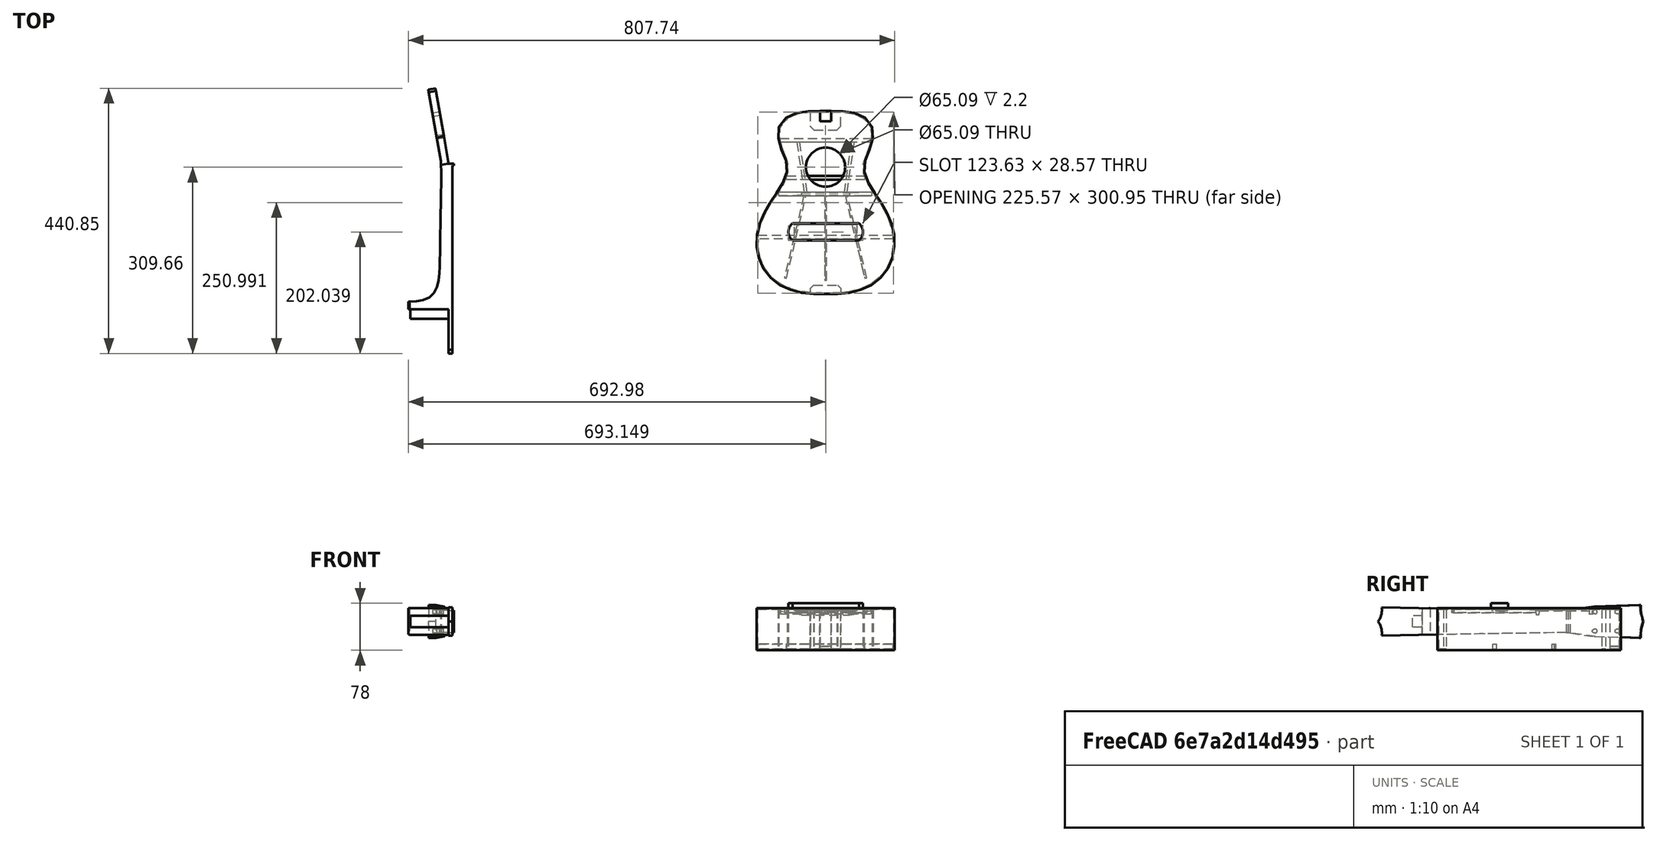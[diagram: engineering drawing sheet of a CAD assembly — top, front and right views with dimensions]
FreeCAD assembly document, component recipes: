
FREECAD ASSEMBLY — COMPONENT RECIPES ("ukulele")

This assembly document has 2 components, labeled P0..P1 below (a component is one placed body or linked part). 2 of them carry a construction recipe — the FreeCAD feature program that regenerates the part from scratch, quoted from this document or its linked companion documents; the rest are supplied as boundary geometry only. No exploded tour is included for this assembly.
COMPONENT P0 — recipe-attached ("kast001", modeled in this document).
Construction recipe (the document's own serialized feature program — sketch geometry with constraints, then the solid features built on it; lengths are millimeters unless a unit is written):

FEATURE [Sketcher::SketchObject] Sketch003  label="vk"
  ArcFitTolerance = 1e-06
  FullyConstrained = false
  MakeInternals = false
  sketch-geometry (68):
    g0: BSplineCurve PolesCount=33 KnotsCount=31 Degree=3 IsPeriodic=0
    g1-g33: Circle [constr] x33 (B-spline internal-alignment scaffolding for g0; pole/knot coordinates omitted)
    g34-g64: GeomPoint [constr] x31 (B-spline internal-alignment scaffolding for g0; pole/knot coordinates omitted)
    g65: BSplineCurve PolesCount=33 KnotsCount=31 Degree=3 IsPeriodic=0
    g66: LineSegment StartX=-9.40108 StartY=93.5875 StartZ=0 EndX=9.40107 EndY=93.5875 EndZ=0
    g67: LineSegment StartX=-0.637124 StartY=-210.927 StartZ=0 EndX=0.637124 EndY=-210.927 EndZ=0
  constraints (73):
    c: InternalAlignment(g1,g0)
    c: Weight(g1) = 1
    c: InternalAlignment(g2,g0)
    c: Equal(g2,g1)
    c: InternalAlignment(g3,g0)
    c: Equal(g3,g1)
    c: InternalAlignment(g4,g0)
    c: Equal(g4,g1)
    c: InternalAlignment(g5,g0)
    c: Equal(g5,g1)
    c: InternalAlignment(g6,g0)
    c: Equal(g6,g1)
    c: InternalAlignment(g7,g0)
    c: Equal(g7,g1)
    c: InternalAlignment(g8,g0)
    c: Equal(g8,g1)
    c: InternalAlignment(g9,g0)
    c: Equal(g9,g1)
    c: InternalAlignment(g10,g0)
    c: Equal(g10,g1)
    c: InternalAlignment(g11,g0)
    c: Equal(g11,g1)
    c: InternalAlignment(g12,g0)
    c: Equal(g12,g1)
    c: InternalAlignment(g13,g0)
    c: Equal(g13,g1)
    c: InternalAlignment(g14,g0)
    c: Equal(g14,g1)
    c: InternalAlignment(g15,g0)
    c: Equal(g15,g1)
    c: InternalAlignment(g16,g0)
    c: Equal(g16,g1)
    c: InternalAlignment(g17,g0)
    c: Equal(g17,g1)
    c: InternalAlignment(g18,g0)
    c: Equal(g18,g1)
    c: InternalAlignment(g19,g0)
    c: Equal(g19,g1)
    c: InternalAlignment(g20,g0)
    c: Equal(g20,g1)
    c: InternalAlignment(g21,g0)
    c: Equal(g21,g1)
    c: InternalAlignment(g22,g0)
    c: Equal(g22,g1)
    c: InternalAlignment(g23,g0)
    c: Equal(g23,g1)
    c: InternalAlignment(g24,g0)
    c: Equal(g24,g1)
    c: InternalAlignment(g25,g0)
    c: Equal(g25,g1)
    c: InternalAlignment(g26,g0)
    c: Equal(g26,g1)
    c: InternalAlignment(g27,g0)
    c: Equal(g27,g1)
    c: InternalAlignment(g28,g0)
    c: Equal(g28,g1)
    c: InternalAlignment(g29,g0)
    c: Equal(g29,g1)
    c: InternalAlignment(g30,g0)
    c: Equal(g30,g1)
    c: InternalAlignment(g31,g0)
    c: Equal(g31,g1)
    c: InternalAlignment(g32,g0)
    c: Equal(g32,g1)
    c: InternalAlignment(g33,g0)
    c: Equal(g33,g1)
    c: InternalAlignment(g34-g64 -> g0) x31
    c: Coincident(g66,g0)
    c: Coincident(g66,g65)
    c: Horizontal(g66)
    c: Coincident(g67,g0)
    c: Coincident(g67,g65)
    c: Horizontal(g67)
FEATURE [PartDesign::Pad] Pad
  Direction = (0,0,1)
  Length = 2.2
  Length2 = 10
  Profile = -> Sketch003
  ReferenceAxis = -> Sketch003 [N_Axis]
  Reversed = true
  Suppressed = false
  Type = 0
  expr: Length = <<dimensies>>.DIKTE_FRONT
FEATURE [Sketcher::SketchObject] Sketch004
  ArcFitTolerance = 1e-06
  AttachmentSupport = -> [XY_Plane001]
  FullyConstrained = true
  MakeInternals = false
  MapMode = 5
  sketch-geometry (1):
    g0: Circle CenterX=0 CenterY=0 CenterZ=0 NormalX=0 NormalY=0 NormalZ=1 AngleXU=0 Radius=32.5435
  constraints (2):
    c: Coincident(g0,g-1)
    c: Diameter(g0) = 65.087
FEATURE [PartDesign::Pocket] Pocket
  BaseFeature = -> Pad
  Direction = (0,0,-1)
  Length = 5
  Length2 = 5
  Profile = -> Sketch004
  ReferenceAxis = -> Sketch004 [N_Axis]
  Suppressed = false
  Type = 2
FEATURE [Sketcher::SketchObject] Sketch005  label="base sketch001"
  ArcFitTolerance = 1e-06
  FullyConstrained = false
  MakeInternals = false
  sketch-geometry (136):
    g0: BSplineCurve PolesCount=33 KnotsCount=31 Degree=3 IsPeriodic=0
    g1-g33: Circle [constr] x33 (B-spline internal-alignment scaffolding for g0; pole/knot coordinates omitted)
    g34-g64: GeomPoint [constr] x31 (B-spline internal-alignment scaffolding for g0; pole/knot coordinates omitted)
    g65: BSplineCurve PolesCount=33 KnotsCount=31 Degree=3 IsPeriodic=0
    g66-g98: Circle [constr] x33 (B-spline internal-alignment scaffolding for g65; pole/knot coordinates omitted)
    g99-g129: GeomPoint [constr] x31 (B-spline internal-alignment scaffolding for g65; pole/knot coordinates omitted)
    g130: BSplineCurve PolesCount=33 KnotsCount=31 Degree=3 IsPeriodic=0
    g131: BSplineCurve PolesCount=33 KnotsCount=31 Degree=3 IsPeriodic=0
    g132: LineSegment StartX=-9.32903 StartY=91.8043 StartZ=0 EndX=9.32903 EndY=91.8043 EndZ=0
    g133: LineSegment StartX=-9.40108 StartY=93.5875 StartZ=0 EndX=9.40107 EndY=93.5875 EndZ=0
    g134: LineSegment StartX=-0.629425 StartY=-209.143 StartZ=0 EndX=0.629425 EndY=-209.143 EndZ=0
    g135: LineSegment StartX=-0.637124 StartY=-210.927 StartZ=0 EndX=0.637124 EndY=-210.927 EndZ=0
  constraints (146):
    c: InternalAlignment(g1,g0)
    c: Weight(g1) = 1
    c: InternalAlignment(g2,g0)
    c: Equal(g2,g1)
    c: InternalAlignment(g3,g0)
    c: Equal(g3,g1)
    c: InternalAlignment(g4,g0)
    c: Equal(g4,g1)
    c: InternalAlignment(g5,g0)
    c: Equal(g5,g1)
    c: InternalAlignment(g6,g0)
    c: Equal(g6,g1)
    c: InternalAlignment(g7,g0)
    c: Equal(g7,g1)
    c: InternalAlignment(g8,g0)
    c: Equal(g8,g1)
    c: InternalAlignment(g9,g0)
    c: Equal(g9,g1)
    c: InternalAlignment(g10,g0)
    c: Equal(g10,g1)
    c: InternalAlignment(g11,g0)
    c: Equal(g11,g1)
    c: InternalAlignment(g12,g0)
    c: Equal(g12,g1)
    c: InternalAlignment(g13,g0)
    c: Equal(g13,g1)
    c: InternalAlignment(g14,g0)
    c: Equal(g14,g1)
    c: InternalAlignment(g15,g0)
    c: Equal(g15,g1)
    c: InternalAlignment(g16,g0)
    c: Equal(g16,g1)
    c: InternalAlignment(g17,g0)
    c: Equal(g17,g1)
    c: InternalAlignment(g18,g0)
    c: Equal(g18,g1)
    c: InternalAlignment(g19,g0)
    c: Equal(g19,g1)
    c: InternalAlignment(g20,g0)
    c: Equal(g20,g1)
    c: InternalAlignment(g21,g0)
    c: Equal(g21,g1)
    c: InternalAlignment(g22,g0)
    c: Equal(g22,g1)
    c: InternalAlignment(g23,g0)
    c: Equal(g23,g1)
    c: InternalAlignment(g24,g0)
    c: Equal(g24,g1)
    c: InternalAlignment(g25,g0)
    c: Equal(g25,g1)
    c: InternalAlignment(g26,g0)
    c: Equal(g26,g1)
    c: InternalAlignment(g27,g0)
    c: Equal(g27,g1)
    c: InternalAlignment(g28,g0)
    c: Equal(g28,g1)
    c: InternalAlignment(g29,g0)
    c: Equal(g29,g1)
    c: InternalAlignment(g30,g0)
    c: Equal(g30,g1)
    c: InternalAlignment(g31,g0)
    c: Equal(g31,g1)
    c: InternalAlignment(g32,g0)
    c: Equal(g32,g1)
    c: InternalAlignment(g33,g0)
    c: Equal(g33,g1)
    c: InternalAlignment(g34-g64 -> g0) x31
    c: InternalAlignment(g66,g65)
    c: Weight(g66) = 1
    c: InternalAlignment(g67,g65)
    c: Equal(g67,g66)
    c: InternalAlignment(g68,g65)
    c: Equal(g68,g66)
    c: InternalAlignment(g69,g65)
    c: Equal(g69,g66)
    c: InternalAlignment(g70,g65)
    c: Equal(g70,g66)
    c: InternalAlignment(g71,g65)
    c: Equal(g71,g66)
    c: InternalAlignment(g72,g65)
    c: Equal(g72,g66)
    c: InternalAlignment(g73,g65)
    c: Equal(g73,g66)
    c: InternalAlignment(g74,g65)
    c: Equal(g74,g66)
    c: InternalAlignment(g75,g65)
    c: Equal(g75,g66)
    c: InternalAlignment(g76,g65)
    c: Equal(g76,g66)
    c: InternalAlignment(g77,g65)
    c: Equal(g77,g66)
    c: InternalAlignment(g78,g65)
    c: Equal(g78,g66)
    c: InternalAlignment(g79,g65)
    c: Equal(g79,g66)
    c: InternalAlignment(g80,g65)
    c: Equal(g80,g66)
    c: InternalAlignment(g81,g65)
    c: Equal(g81,g66)
    c: InternalAlignment(g82,g65)
    c: Equal(g82,g66)
    c: InternalAlignment(g83,g65)
    c: Equal(g83,g66)
    c: InternalAlignment(g84,g65)
    c: Equal(g84,g66)
    c: InternalAlignment(g85,g65)
    c: Equal(g85,g66)
    c: InternalAlignment(g86,g65)
    c: Equal(g86,g66)
    c: InternalAlignment(g87,g65)
    c: Equal(g87,g66)
    c: InternalAlignment(g88,g65)
    c: Equal(g88,g66)
    c: InternalAlignment(g89,g65)
    c: Equal(g89,g66)
    c: InternalAlignment(g90,g65)
    c: Equal(g90,g66)
    c: InternalAlignment(g91,g65)
    c: Equal(g91,g66)
    c: InternalAlignment(g92,g65)
    c: Equal(g92,g66)
    c: InternalAlignment(g93,g65)
    c: Equal(g93,g66)
    c: InternalAlignment(g94,g65)
    c: Equal(g94,g66)
    c: InternalAlignment(g95,g65)
    c: Equal(g95,g66)
    c: InternalAlignment(g96,g65)
    c: Equal(g96,g66)
    c: InternalAlignment(g97,g65)
    c: Equal(g97,g66)
    c: InternalAlignment(g98,g65)
    c: Equal(g98,g66)
    c: InternalAlignment(g99-g129 -> g65) x31
    c: Coincident(g132,g65)
    c: Coincident(g132,g131)
    c: Horizontal(g132)
    c: Coincident(g133,g0)
    c: Coincident(g133,g130)
    c: Horizontal(g133)
    c: Coincident(g134,g65)
    c: Coincident(g134,g131)
    c: Horizontal(g134)
    c: Coincident(g135,g0)
    c: Coincident(g135,g130)
    c: Horizontal(g135)
FEATURE [PartDesign::Pad] Pad001
  BaseFeature = -> Pocket
  Direction = (0,0,1)
  Length = 70
  Length2 = 10
  Profile = -> Sketch005
  ReferenceAxis = -> Sketch005 [N_Axis]
  Refine = true
  Reversed = true
  Suppressed = false
  Type = 0
  expr: Length = 70
FEATURE [Sketcher::SketchObject] Sketch006
  ArcFitTolerance = 1e-06
  AttachmentSupport = -> [YZ_Plane001]
  ExternalGeometry = -> [Pad001]
  FullyConstrained = true
  MakeInternals = false
  MapMode = 5
  Placement = pos=(0,0,0) rot=(0.57735,0.57735,0.57735;2.0944rad)
  sketch-geometry (10):
    g0: GeomPoint X=0 Y=-2.2 Z=0
    g1: GeomPoint X=-44.45 Y=-2.2 Z=0
    g2: GeomPoint X=44.45 Y=-2.2 Z=0
    g3: LineSegment StartX=-47.625 StartY=-2.2 StartZ=0 EndX=-41.275 EndY=-2.2 EndZ=0
    g4: LineSegment StartX=-41.275 StartY=-2.2 StartZ=0 EndX=-41.275 EndY=-7.2 EndZ=0
    g5: LineSegment StartX=-41.275 StartY=-7.2 StartZ=0 EndX=-42.45 EndY=-11.725 EndZ=0
    g6: LineSegment StartX=-42.45 StartY=-11.725 StartZ=0 EndX=-46.45 EndY=-11.725 EndZ=0
    g7: LineSegment StartX=-46.45 StartY=-11.725 StartZ=0 EndX=-47.625 EndY=-7.2 EndZ=0
    g8: LineSegment StartX=-47.625 StartY=-7.2 StartZ=0 EndX=-47.625 EndY=-2.2 EndZ=0
    g9: GeomPoint X=-44.45 Y=-11.725 Z=0
  constraints (24):
    c: PointOnObject(g0,g-4)
    c: PointOnObject(g1,g-4)
    c: DistanceX(g1,g0) = 44.45
    c: Symmetric(g1,g2,g0)
    c: PointOnObject(g0,g-2)
    c: PointOnObject(g3,g-4)
    c: PointOnObject(g3,g-4)
    c: Coincident(g3,g4)
    c: Vertical(g4)
    c: Coincident(g4,g5)
    c: Coincident(g5,g6)
    c: Horizontal(g6)
    c: Coincident(g6,g7)
    c: Coincident(g7,g8)
    c: Coincident(g8,g3)
    c: Symmetric(g3,g3,g1)
    c: Vertical(g8)
    c: DistanceX(g3,g3) = 6.35
    c: Horizontal(g4,g7)
    c: DistanceY(g5,g3) = 9.525
    c: DistanceY(g8,g8) = 5
    c: Symmetric(g6,g6,g9)
    c: Vertical(g9,g1)
    c: DistanceX(g6,g9) = 2
FEATURE [PartDesign::Pad] Pad002
  BaseFeature = -> Pad001
  Direction = (1,0,0)
  Length = 155
  Length2 = 10
  Midplane = true
  Profile = -> Sketch006
  ReferenceAxis = -> Sketch006 [N_Axis]
  Refine = true
  Suppressed = false
  Type = 0
FEATURE [Sketcher::SketchObject] Sketch007
  ArcFitTolerance = 1e-06
  AttachmentSupport = -> [Pad002]
  ExternalGeometry = -> [Pad002]
  FullyConstrained = true
  MakeInternals = false
  MapMode = 5
  Placement = pos=(0,-41.275,0) rot=(0,0.707107,0.707107;3.14159rad)
  sketch-geometry (12):
    g0: GeomPoint X=40 Y=-11.725 Z=0
    g1: GeomPoint X=-40 Y=-11.725 Z=0
    g2: GeomPoint X=0 Y=-7.2 Z=0
    g3: GeomPoint X=-78.3882 Y=-4.2 Z=0
    g4: GeomPoint X=78.3882 Y=-4.2 Z=0
    g5: LineSegment StartX=78.3882 StartY=-4.2 StartZ=0 EndX=40 EndY=-11.725 EndZ=0
    g6: LineSegment StartX=-40 StartY=-11.725 StartZ=0 EndX=-78.3882 EndY=-4.2 EndZ=0
    g7: LineSegment StartX=40 StartY=-11.725 StartZ=0 EndX=-40 EndY=-11.725 EndZ=0
    g8: LineSegment StartX=78.3882 StartY=-4.2 StartZ=0 EndX=78.3882 EndY=-24.2 EndZ=0
    g9: LineSegment StartX=78.3882 StartY=-24.2 StartZ=0 EndX=-78.3882 EndY=-24.2 EndZ=0
    g10: LineSegment StartX=-78.3882 StartY=-4.2 StartZ=0 EndX=-78.3882 EndY=-24.2 EndZ=0
    g11: GeomPoint X=0 Y=-11.725 Z=0
  constraints (24):
    c: Symmetric(g-4,g-4,g2)
    c: PointOnObject(g3,g-6)
    c: PointOnObject(g4,g-5)
    c: Horizontal(g4,g3)
    c: DistanceX(g2,g0) = 40
    c: Coincident(g5,g4)
    c: Coincident(g5,g0)
    c: Coincident(g6,g1)
    c: DistanceY(g4,g-5) = 2
    c: Coincident(g7,g0)
    c: Coincident(g7,g1)
    c: Coincident(g8,g4)
    c: Vertical(g8)
    c: Coincident(g9,g8)
    c: Horizontal(g9)
    c: Coincident(g10,g9)
    c: Vertical(g10)
    c: DistanceY(g10,g10) = 20
    c: Coincident(g3,g10)
    c: Coincident(g3,g6)
    c: PointOnObject(g11,g-7)
    c: PointOnObject(g11,g-2)
    c: Symmetric(g1,g0,g11)
    c: Horizontal(g7)
FEATURE [PartDesign::Pocket] Pocket001
  BaseFeature = -> Pad002
  Direction = (0,-1,2e-16)
  Length = 9
  Length2 = 5
  Profile = -> Sketch007
  ReferenceAxis = -> Sketch007 [N_Axis]
  Refine = true
  Suppressed = false
  Type = 0
FEATURE [Sketcher::SketchObject] Sketch008
  ArcFitTolerance = 1e-06
  AttachmentSupport = -> [Pocket001]
  ExternalGeometry = -> [Pocket001]
  FullyConstrained = true
  MakeInternals = false
  MapMode = 5
  Placement = pos=(0,0,-2.2) rot=(1,0,0;3.14159rad)
  sketch-geometry (8):
    g0: LineSegment StartX=-25 StartY=209.143 StartZ=0 EndX=25 EndY=209.143 EndZ=0
    g1: GeomPoint X=-2.2048e-07 Y=209.143 Z=0
    g2: LineSegment StartX=-25 StartY=209.143 StartZ=0 EndX=-25 EndY=201.143 EndZ=0
    g3: LineSegment StartX=-25 StartY=201.143 StartZ=0 EndX=-20 EndY=196.143 EndZ=0
    g4: LineSegment StartX=-20 StartY=196.143 StartZ=0 EndX=20 EndY=196.143 EndZ=0
    g5: LineSegment StartX=20 StartY=196.143 StartZ=0 EndX=25 EndY=201.143 EndZ=0
    g6: LineSegment StartX=25 StartY=201.143 StartZ=0 EndX=25 EndY=209.143 EndZ=0
    g7: GeomPoint X=0 Y=196.143 Z=0
  constraints (19):
    c: Horizontal(g0)
    c: Symmetric(g0,g0,g1)
    c: Symmetric(g-4,g-3,g1)
    c: DistanceX(g0,g0) = 50
    c: Coincident(g0,g2)
    c: Vertical(g2)
    c: Coincident(g2,g3)
    c: Coincident(g3,g4)
    c: Horizontal(g4)
    c: Coincident(g4,g5)
    c: Coincident(g5,g6)
    c: Coincident(g6,g0)
    c: Vertical(g6)
    c: Symmetric(g4,g4,g7)
    c: PointOnObject(g7,g-2)
    c: Angle(g3,g2) = 2.35619
    c: DistanceY(g6,g6) = 8
    c: DistanceX(g4,g4) = 40
    c: Horizontal(g2,g5)
FEATURE [PartDesign::Pad] Pad003
  BaseFeature = -> Pocket001
  Direction = (0,0,-1)
  Length = 65.6
  Length2 = 10
  Profile = -> Sketch008
  ReferenceAxis = -> Sketch008 [N_Axis]
  Refine = true
  Suppressed = false
  Type = 0
  expr: Length = <<dimensies>>.DIEPTE - 2 * <<dimensies>>.DIKTE_FRONT
FEATURE [Sketcher::SketchObject] Sketch009
  ArcFitTolerance = 1e-06
  AttachmentSupport = -> [Pad003]
  FullyConstrained = true
  MakeInternals = false
  MapMode = 5
  Placement = pos=(0,0,-2.2) rot=(1,0,0;3.14159rad)
  sketch-geometry (12):
    g0: LineSegment StartX=-25.4 StartY=-92.925 StartZ=0 EndX=-25.4 EndY=-68.289 EndZ=0
    g1: LineSegment StartX=-25.4 StartY=-68.289 StartZ=0 EndX=-19.036 EndY=-61.925 EndZ=0
    g2: LineSegment StartX=-19.036 StartY=-61.925 StartZ=0 EndX=19.036 EndY=-61.925 EndZ=0
    g3: LineSegment StartX=19.036 StartY=-61.925 StartZ=0 EndX=25.4 EndY=-68.289 EndZ=0
    g4: LineSegment StartX=25.4 StartY=-68.289 StartZ=0 EndX=25.4 EndY=-92.925 EndZ=0
    g5: LineSegment StartX=25.4 StartY=-92.925 StartZ=0 EndX=9.525 EndY=-92.925 EndZ=0
    g6: LineSegment StartX=9.525 StartY=-92.925 StartZ=0 EndX=9.525 EndY=-75.525 EndZ=0
    g7: LineSegment StartX=9.525 StartY=-75.525 StartZ=0 EndX=-9.525 EndY=-75.525 EndZ=0
    g8: LineSegment StartX=-9.525 StartY=-75.525 StartZ=0 EndX=-9.525 EndY=-92.925 EndZ=0
    g9: LineSegment StartX=-9.525 StartY=-92.925 StartZ=0 EndX=-25.4 EndY=-92.925 EndZ=0
    g10: GeomPoint X=0 Y=-61.925 Z=0
    g11: GeomPoint X=0 Y=-75.525 Z=0
  constraints (32):
    c: Vertical(g0)
    c: Coincident(g0,g1)
    c: Coincident(g1,g2)
    c: Horizontal(g2)
    c: Coincident(g2,g3)
    c: Coincident(g3,g4)
    c: Vertical(g4)
    c: Coincident(g4,g5)
    c: Horizontal(g5)
    c: Coincident(g5,g6)
    c: Vertical(g6)
    c: Coincident(g6,g7)
    c: Horizontal(g7)
    c: Coincident(g7,g8)
    c: Vertical(g8)
    c: Coincident(g8,g9)
    c: Coincident(g9,g0)
    c: Horizontal(g9)
    c: Symmetric(g2,g2,g10)
    c: Symmetric(g7,g7,g11)
    c: PointOnObject(g11,g-2)
    c: PointOnObject(g10,g-2)
    c: Angle(g0,g1) = 2.35619
    c: Horizontal(g3,g0)
    c: Equal(g9,g5)
    c: DistanceX(g8,g5) = 19.05
    c: DistanceY(g0,g1) = 31
    c: DistanceY(g8,g8) = 17.4
    c: Horizontal(g8,g5)
    c: DistanceX(g0,g4) = 50.8
    c: Distance(g1,g1) = 9
    c: Block(g2)
FEATURE [PartDesign::Pad] Pad004
  BaseFeature = -> Pad003
  Direction = (0,0,-1)
  Length = 65.6
  Length2 = 10
  Profile = -> Sketch009
  ReferenceAxis = -> Sketch009 [N_Axis]
  Refine = true
  Suppressed = false
  Type = 0
  expr: Length = <<dimensies>>.DIEPTE - 2 * <<dimensies>>.DIKTE_FRONT
FEATURE [Sketcher::SketchObject] Sketch010
  ArcFitTolerance = 1e-06
  AttachmentSupport = -> [Pad004]
  ExternalGeometry = -> [Pad004,Sketch003]
  FullyConstrained = true
  MakeInternals = false
  MapMode = 5
  Placement = pos=(0,93.5875,0) rot=(0,0.707107,0.707107;3.14159rad)
  sketch-geometry (4):
    g0: LineSegment StartX=-9.40107 StartY=0 StartZ=0 EndX=-9.40107 EndY=-63.5 EndZ=0
    g1: LineSegment StartX=-9.40107 StartY=-63.5 StartZ=0 EndX=9.40108 EndY=-63.5 EndZ=0
    g2: LineSegment StartX=9.40108 StartY=-63.5 StartZ=0 EndX=9.40108 EndY=0 EndZ=0
    g3: LineSegment StartX=9.40108 StartY=0 StartZ=0 EndX=-9.40107 EndY=0 EndZ=0
  constraints (10):
    c: Coincident(g0,g1)
    c: Coincident(g1,g2)
    c: Coincident(g2,g3)
    c: Coincident(g3,g0)
    c: Vertical(g0)
    c: Vertical(g2)
    c: Horizontal(g1)
    c: Coincident(g0,g-6)
    c: Coincident(g-6,g2)
    c: DistanceY(g0,g0) = 63.5
FEATURE [PartDesign::Pocket] Pocket002
  BaseFeature = -> Pad004
  Direction = (0,-1,2e-16)
  Length = 17.5
  Length2 = 5
  Profile = -> Sketch010
  ReferenceAxis = -> Sketch010 [N_Axis]
  Refine = true
  Suppressed = false
  Type = 0
FEATURE [Sketcher::SketchObject] Sketch011
  ArcFitTolerance = 1e-06
  AttachmentSupport = -> [Pocket002]
  FullyConstrained = false
  MakeInternals = false
  MapMode = 5
  Placement = pos=(0,0,-2.2) rot=(1,0,0;3.14159rad)
  sketch-geometry (6):
    g0: LineSegment StartX=-52 StartY=120.048 StartZ=0 EndX=-52 EndY=95.0481 EndZ=0
    g1: LineSegment StartX=-52 StartY=95.0481 StartZ=0 EndX=52 EndY=95.0481 EndZ=0
    g2: LineSegment StartX=52 StartY=95.0481 StartZ=0 EndX=52 EndY=120.048 EndZ=0
    g3: LineSegment StartX=52 StartY=120.048 StartZ=0 EndX=-52 EndY=120.048 EndZ=0
    g4: GeomPoint X=1e-16 Y=120.048 Z=0
    g5: GeomPoint X=0 Y=105.469 Z=0
  constraints (13):
    c: Coincident(g0,g1)
    c: Coincident(g1,g2)
    c: Coincident(g2,g3)
    c: Coincident(g3,g0)
    c: Vertical(g0)
    c: Vertical(g2)
    c: Horizontal(g3)
    c: PointOnObject(g5,g-2)
    c: Symmetric(g0,g2,g4)
    c: Symmetric(g1,g0,g-2)
    c: DistanceY(g0,g0) = 25
    c: DistanceX(g3,g3) = 104
    c: Block(g3)
FEATURE [PartDesign::Pad] Pad005
  BaseFeature = -> Pocket002
  Direction = (0,0,-1)
  Length = 2.2
  Length2 = 10
  Profile = -> Sketch011
  ReferenceAxis = -> Sketch011 [N_Axis]
  Refine = true
  Suppressed = false
  Type = 0
  expr: Length = <<dimensies>>.DIKTE_FRONT
FEATURE [Sketcher::SketchObject] Sketch012
  ArcFitTolerance = 1e-06
  AttachmentSupport = -> [Pad005]
  FullyConstrained = true
  MakeInternals = false
  MapMode = 5
  sketch-geometry (5):
    g0: LineSegment StartX=-54.9901 StartY=-93.3363 StartZ=0 EndX=55.5099 EndY=-93.3363 EndZ=0
    g1: LineSegment StartX=-54.9901 StartY=-121.906 StartZ=0 EndX=55.5099 EndY=-121.906 EndZ=0
    g2: ArcOfCircle CenterX=-42.9824 CenterY=-107.621 CenterZ=0 NormalX=0 NormalY=0 NormalZ=1 AngleXU=0 Radius=18.6613 StartAngle=2.26979 EndAngle=4.01339
    g3: ArcOfCircle CenterX=42.9824 CenterY=-107.621 CenterZ=0 NormalX=0 NormalY=0 NormalZ=1 AngleXU=0 Radius=19 StartAngle=5.43233 EndAngle=7.13404
    g4: GeomPoint X=0 Y=-107.621 Z=0
  constraints (14):
    c: Horizontal(g0)
    c: Horizontal(g1)
    c: Coincident(g2,g0)
    c: Coincident(g2,g1)
    c: Coincident(g3,g0)
    c: Coincident(g3,g1)
    c: DistanceY(g1,g2) = 28.57
    c: DistanceX(g0,g0) = 110.5
    c: Horizontal(g3,g2)
    c: PointOnObject(g4,g-2)
    c: Symmetric(g2,g3,g4)
    c: Radius(g3) = 19
    c: Vertical(g1,g0)
    c: Block(g0)
FEATURE [PartDesign::Pad] Pad006
  BaseFeature = -> Pad005
  Direction = (0,0,1)
  Length = 8
  Length2 = 10
  Profile = -> Sketch012
  ReferenceAxis = -> Sketch012 [N_Axis]
  Refine = true
  Suppressed = false
  Type = 0
FEATURE [Sketcher::SketchObject] Sketch015
  ArcFitTolerance = 1e-06
  AttachmentSupport = -> [Pad006]
  ExternalGeometry = -> [Pad006]
  FullyConstrained = true
  MakeInternals = false
  MapMode = 5
  Placement = pos=(0,0,-67.8) rot=(1,0,0;3.14159rad)
  sketch-geometry (4):
    g0: LineSegment StartX=-9.32903 StartY=-91.8043 StartZ=0 EndX=9.40107 EndY=-91.8043 EndZ=0
    g1: LineSegment StartX=9.40107 StartY=-91.8043 StartZ=0 EndX=9.40107 EndY=-76.0875 EndZ=0
    g2: LineSegment StartX=9.40107 StartY=-76.0875 StartZ=0 EndX=-9.32903 EndY=-76.0875 EndZ=0
    g3: LineSegment StartX=-9.32903 StartY=-76.0875 StartZ=0 EndX=-9.32903 EndY=-91.8043 EndZ=0
  constraints (10):
    c: Coincident(g0,g1)
    c: Coincident(g1,g2)
    c: Coincident(g2,g3)
    c: Coincident(g3,g0)
    c: Horizontal(g0)
    c: Horizontal(g2)
    c: Vertical(g1)
    c: Vertical(g3)
    c: Coincident(g0,g-3)
    c: Coincident(g1,g-4)
FEATURE [PartDesign::Pad] Pad009
  BaseFeature = -> Pad006
  Direction = (0,0,-1)
  Length = 10
  Length2 = 10
  Profile = -> Sketch015
  ReferenceAxis = -> Sketch015 [N_Axis]
  Refine = true
  Reversed = true
  Suppressed = false
  Type = 3
  UpToFace = -> Pad006 [Face9]
FEATURE [Sketcher::SketchObject] Sketch046  label="bracing_master"
  ArcFitTolerance = 1e-06
  AttachmentSupport = -> [Pad009]
  ExternalGeometry = -> [Pad009]
  FullyConstrained = false
  MakeInternals = false
  MapMode = 5
  Placement = pos=(0,0,-2.2) rot=(1,0,0;3.14159rad)
  sketch-geometry (29):
    g0: LineSegment StartX=-75.375 StartY=-41.175 StartZ=0 EndX=75.375 EndY=-41.175 EndZ=0
    g1: LineSegment [constr] StartX=-4.8e-15 StartY=41.275 StartZ=0 EndX=-4.8e-15 EndY=-41.175 EndZ=0
    g2: LineSegment StartX=-75.375 StartY=-41.175 StartZ=0 EndX=-75.375 EndY=-47.525 EndZ=0
    g3: LineSegment StartX=-75.375 StartY=-47.525 StartZ=0 EndX=75.375 EndY=-47.525 EndZ=0
    g4: LineSegment StartX=75.375 StartY=-47.525 StartZ=0 EndX=75.375 EndY=-41.175 EndZ=0
    g5: LineSegment StartX=-1.6 StartY=187.625 StartZ=0 EndX=-1.6 EndY=47.625 EndZ=0
    g6: LineSegment StartX=-1.6 StartY=47.625 StartZ=0 EndX=1.6 EndY=47.625 EndZ=0
    g7: LineSegment StartX=1.6 StartY=47.625 StartZ=0 EndX=1.6 EndY=187.625 EndZ=0
    g8: LineSegment StartX=1.6 StartY=187.625 StartZ=0 EndX=-1.6 EndY=187.625 EndZ=0
    g9: GeomPoint X=-5.4e-15 Y=47.625 Z=0
    g10: LineSegment StartX=-30.75 StartY=41.275 StartZ=0 EndX=-42.75 EndY=-41.175 EndZ=0
    g11: LineSegment StartX=-47.8027 StartY=-41.175 StartZ=0 EndX=-35.8027 EndY=41.275 EndZ=0
    g12: LineSegment StartX=-35.8027 StartY=41.275 StartZ=0 EndX=-30.75 EndY=41.275 EndZ=0
    g13: LineSegment StartX=-47.8027 StartY=-41.175 StartZ=0 EndX=-42.75 EndY=-41.175 EndZ=0
    g14: LineSegment StartX=30.75 StartY=41.275 StartZ=0 EndX=42.75 EndY=-41.175 EndZ=0
    g15: LineSegment StartX=42.75 StartY=-41.175 StartZ=0 EndX=47.8027 EndY=-41.175 EndZ=0
    g16: LineSegment StartX=47.8027 StartY=-41.175 StartZ=0 EndX=35.8027 EndY=41.275 EndZ=0
    g17: LineSegment StartX=35.8027 StartY=41.275 StartZ=0 EndX=30.75 EndY=41.275 EndZ=0
    g18: LineSegment StartX=-32.6 StartY=47.625 StartZ=0 EndX=-65.0942 EndY=184.83 EndZ=0
    g19: LineSegment StartX=-65.0942 StartY=184.83 StartZ=0 EndX=-68.5 EndY=184.023 EndZ=0
    g20: LineSegment StartX=-68.5 StartY=184.023 StartZ=0 EndX=-36.1968 EndY=47.625 EndZ=0
    g21: LineSegment StartX=-36.1968 StartY=47.625 StartZ=0 EndX=-32.6 EndY=47.625 EndZ=0
    g22: LineSegment StartX=36.1968 StartY=47.625 StartZ=0 EndX=68.5 EndY=184.023 EndZ=0
    g23: LineSegment StartX=68.5 StartY=184.023 StartZ=0 EndX=65.0942 EndY=184.83 EndZ=0
    g24: LineSegment StartX=65.0942 StartY=184.83 StartZ=0 EndX=32.6 EndY=47.625 EndZ=0
    g25: LineSegment StartX=32.6 StartY=47.625 StartZ=0 EndX=36.1968 EndY=47.625 EndZ=0
    g26: LineSegment [constr] StartX=-68.5 StartY=184.023 StartZ=0 EndX=68.5 EndY=184.023 EndZ=0
    g27: GeomPoint [constr] X=0 Y=184.023 Z=0
    g28: LineSegment [constr] StartX=-35.0311 StartY=11.8606 StartZ=0 EndX=-39.9789 EndY=12.5807 EndZ=0
  constraints (75):
    c: Horizontal(g0)
    c: Symmetric(g-3,g-3,g1)
    c: Symmetric(g0,g0,g1)
    c: Vertical(g1)
    c: Coincident(g2,g0)
    c: Vertical(g2)
    c: Coincident(g3,g2)
    c: Horizontal(g3)
    c: Coincident(g4,g3)
    c: Coincident(g4,g0)
    c: Vertical(g4)
    c: Equal(g2,g-4)
    c: DistanceY(g1,g1) = 82.45
    c: DistanceX(g0,g0) = 150.75
    c: Coincident(g5,g6)
    c: Coincident(g6,g7)
    c: Coincident(g7,g8)
    c: Coincident(g8,g5)
    c: Vertical(g5)
    c: Vertical(g7)
    c: Horizontal(g6)
    c: Horizontal(g8)
    c: Symmetric(g6,g6,g9)
    c: Symmetric(g-4,g-5,g9)
    c: DistanceX(g8,g8) = 3.2
    c: DistanceY(g5,g5) = 140
    c: PointOnObject(g10,g-3)
    c: PointOnObject(g10,g0)
    c: PointOnObject(g11,g0)
    c: PointOnObject(g11,g-3)
    c: Coincident(g12,g11)
    c: Coincident(g12,g10)
    c: Coincident(g13,g11)
    c: Coincident(g13,g10)
    c: Coincident(g15,g14)
    c: Coincident(g16,g15)
    c: PointOnObject(g16,g-3)
    c: Coincident(g17,g16)
    c: Coincident(g17,g14)
    c: PointOnObject(g18,g-6)
    c: Coincident(g19,g18)
    c: Coincident(g20,g19)
    c: PointOnObject(g20,g-6)
    c: Coincident(g21,g20)
    c: Coincident(g21,g18)
    c: Coincident(g23,g22)
    c: Coincident(g24,g23)
    c: Coincident(g25,g24)
    c: Coincident(g25,g22)
    c: Symmetric(g18,g24,g9)
    c: Symmetric(g20,g22,g9)
    c: Coincident(g26,g19)
    c: Coincident(g26,g22)
    c: Horizontal(g26)
    c: Symmetric(g26,g26,g27)
    c: PointOnObject(g27,g-2)
    c: Perpendicular(g19,g18)
    c: Perpendicular(g23,g22)
    c: Equal(g19,g23)
    c: Parallel(g18,g20)
    c: DistanceX(g18,g5) = 31
    c: Distance(g19,g19) = 3.5
    c: DistanceX(g26,g26) = 137
    c: Distance(g18,g18) = 141
    c: Parallel(g11,g10)
    c: Parallel(g14,g16)
    c: DistanceX(g10,g14) = 61.5
    c: DistanceX(g10,g14) = 85.5
    c: Symmetric(g10,g14,g1)
    c: Symmetric(g10,g14,g1)
    c: Symmetric(g11,g15,g1)
    c: PointOnObject(g28,g10)
    c: PointOnObject(g28,g11)
    c: Perpendicular(g28,g10)
    c: Distance(g28) = 5
FEATURE [Sketcher::SketchObject] Sketch047
  ArcFitTolerance = 1e-06
  AttachmentSupport = -> [Pad009]
  ExternalGeometry = -> [Sketch046]
  FullyConstrained = true
  MakeInternals = false
  MapMode = 5
  Placement = pos=(0,0,-2.2) rot=(1,0,0;3.14159rad)
  sketch-geometry (4):
    g0: LineSegment StartX=-75.375 StartY=-41.175 StartZ=0 EndX=-75.375 EndY=-47.525 EndZ=0
    g1: LineSegment StartX=-75.375 StartY=-47.525 StartZ=0 EndX=75.375 EndY=-47.525 EndZ=0
    g2: LineSegment StartX=75.375 StartY=-47.525 StartZ=0 EndX=75.375 EndY=-41.175 EndZ=0
    g3: LineSegment StartX=75.375 StartY=-41.175 StartZ=0 EndX=-75.375 EndY=-41.175 EndZ=0
  constraints (8):
    c: Coincident(g-4,g0)
    c: Coincident(g0,g-5)
    c: Coincident(g0,g1)
    c: Coincident(g1,g-6)
    c: Coincident(g1,g2)
    c: Coincident(g2,g-6)
    c: Coincident(g2,g3)
    c: Coincident(g3,g0)
FEATURE [PartDesign::Pad] Pad030
  BaseFeature = -> Pad009
  Direction = (0,0,-1)
  Length = 8
  Length2 = 10
  Profile = -> Sketch047
  ReferenceAxis = -> Sketch047 [N_Axis]
  Refine = true
  Suppressed = false
  Type = 0
FEATURE [Sketcher::SketchObject] Sketch048
  ArcFitTolerance = 1e-06
  AttachmentSupport = -> [Pad030]
  ExternalGeometry = -> [Sketch046]
  FullyConstrained = true
  MakeInternals = false
  MapMode = 5
  Placement = pos=(0,0,-2.2) rot=(1,0,0;3.14159rad)
  sketch-geometry (8):
    g0: LineSegment StartX=-35.8027 StartY=41.275 StartZ=0 EndX=-30.75 EndY=41.275 EndZ=0
    g1: LineSegment StartX=-30.75 StartY=41.275 StartZ=0 EndX=-42.75 EndY=-41.175 EndZ=0
    g2: LineSegment StartX=-42.75 StartY=-41.175 StartZ=0 EndX=-47.8027 EndY=-41.175 EndZ=0
    g3: LineSegment StartX=-47.8027 StartY=-41.175 StartZ=0 EndX=-35.8027 EndY=41.275 EndZ=0
    g4: LineSegment StartX=30.75 StartY=41.275 StartZ=0 EndX=35.8027 EndY=41.275 EndZ=0
    g5: LineSegment StartX=35.8027 StartY=41.275 StartZ=0 EndX=47.8027 EndY=-41.175 EndZ=0
    g6: LineSegment StartX=47.8027 StartY=-41.175 StartZ=0 EndX=42.75 EndY=-41.175 EndZ=0
    g7: LineSegment StartX=42.75 StartY=-41.175 StartZ=0 EndX=30.75 EndY=41.275 EndZ=0
  constraints (16):
    c: Coincident(g-3,g0)
    c: Coincident(g0,g-4)
    c: Coincident(g0,g1)
    c: Coincident(g1,g-4)
    c: Coincident(g1,g2)
    c: Coincident(g2,g-3)
    c: Coincident(g2,g3)
    c: Coincident(g3,g0)
    c: Coincident(g-5,g4)
    c: Coincident(g4,g-6)
    c: Coincident(g4,g5)
    c: Coincident(g5,g-6)
    c: Coincident(g5,g6)
    c: Coincident(g6,g-5)
    c: Coincident(g6,g7)
    c: Coincident(g7,g4)
FEATURE [PartDesign::Pad] Pad031
  BaseFeature = -> Pad030
  Direction = (0,0,-1)
  Length = 2
  Length2 = 10
  Profile = -> Sketch048
  ReferenceAxis = -> Sketch048 [N_Axis]
  Refine = true
  Suppressed = false
  Type = 0
FEATURE [Sketcher::SketchObject] Sketch049
  ArcFitTolerance = 1e-06
  AttachmentSupport = -> [Pad031]
  ExternalGeometry = -> [Sketch046]
  FullyConstrained = true
  MakeInternals = false
  MapMode = 5
  Placement = pos=(0,0,-2.2) rot=(1,0,0;3.14159rad)
  sketch-geometry (12):
    g0: LineSegment StartX=-68.5 StartY=184.023 StartZ=0 EndX=-65.0942 EndY=184.83 EndZ=0
    g1: LineSegment StartX=-65.0942 StartY=184.83 StartZ=0 EndX=-32.6 EndY=47.625 EndZ=0
    g2: LineSegment StartX=-32.6 StartY=47.625 StartZ=0 EndX=-36.1968 EndY=47.625 EndZ=0
    g3: LineSegment StartX=-36.1968 StartY=47.625 StartZ=0 EndX=-68.5 EndY=184.023 EndZ=0
    g4: LineSegment StartX=-1.6 StartY=187.625 StartZ=0 EndX=1.6 EndY=187.625 EndZ=0
    g5: LineSegment StartX=1.6 StartY=187.625 StartZ=0 EndX=1.6 EndY=47.625 EndZ=0
    g6: LineSegment StartX=1.6 StartY=47.625 StartZ=0 EndX=-1.6 EndY=47.625 EndZ=0
    g7: LineSegment StartX=-1.6 StartY=47.625 StartZ=0 EndX=-1.6 EndY=187.625 EndZ=0
    g8: LineSegment StartX=65.0942 StartY=184.83 StartZ=0 EndX=68.5 EndY=184.023 EndZ=0
    g9: LineSegment StartX=68.5 StartY=184.023 StartZ=0 EndX=36.1968 EndY=47.625 EndZ=0
    g10: LineSegment StartX=36.1968 StartY=47.625 StartZ=0 EndX=32.6 EndY=47.625 EndZ=0
    g11: LineSegment StartX=32.6 StartY=47.625 StartZ=0 EndX=65.0942 EndY=184.83 EndZ=0
  constraints (24):
    c: Coincident(g-3,g0)
    c: Coincident(g0,g-4)
    c: Coincident(g0,g1)
    c: Coincident(g1,g-4)
    c: Coincident(g1,g2)
    c: Coincident(g2,g-3)
    c: Coincident(g2,g3)
    c: Coincident(g3,g0)
    c: Coincident(g-5,g4)
    c: Coincident(g4,g-6)
    c: Coincident(g4,g5)
    c: Coincident(g5,g-6)
    c: Coincident(g5,g6)
    c: Coincident(g6,g-5)
    c: Coincident(g6,g7)
    c: Coincident(g7,g4)
    c: Coincident(g-7,g8)
    c: Coincident(g8,g-8)
    c: Coincident(g8,g9)
    c: Coincident(g9,g-8)
    c: Coincident(g9,g10)
    c: Coincident(g10,g-7)
    c: Coincident(g10,g11)
    c: Coincident(g11,g8)
FEATURE [PartDesign::Pad] Pad032
  BaseFeature = -> Pad031
  Direction = (0,0,-1)
  Length = 5.5
  Length2 = 10
  Profile = -> Sketch049
  ReferenceAxis = -> Sketch049 [N_Axis]
  Refine = true
  Suppressed = false
  Type = 0
FEATURE [Sketcher::SketchObject] Sketch050
  ArcFitTolerance = 1e-06
  AttachmentSupport = -> [Pad032]
  ExternalGeometry = -> [Pad032]
  FullyConstrained = true
  MakeInternals = false
  MapMode = 5
  Placement = pos=(0,0,-67.8) rot=(1,0,0;3.14159rad)
  sketch-geometry (12):
    g0: LineSegment StartX=-65 StartY=20.6875 StartZ=0 EndX=-65 EndY=14.3375 EndZ=0
    g1: LineSegment StartX=-65 StartY=14.3375 StartZ=0 EndX=65 EndY=14.3375 EndZ=0
    g2: LineSegment StartX=65 StartY=14.3375 StartZ=0 EndX=65 EndY=20.6875 EndZ=0
    g3: LineSegment StartX=65 StartY=20.6875 StartZ=0 EndX=-65 EndY=20.6875 EndZ=0
    g4: LineSegment StartX=-113 StartY=119.087 StartZ=0 EndX=-113 EndY=112.737 EndZ=0
    g5: LineSegment StartX=-113 StartY=112.737 StartZ=0 EndX=113 EndY=112.737 EndZ=0
    g6: LineSegment StartX=113 StartY=112.737 StartZ=0 EndX=113 EndY=119.087 EndZ=0
    g7: LineSegment StartX=113 StartY=119.087 StartZ=0 EndX=-113 EndY=119.087 EndZ=0
    g8: GeomPoint X=-65 Y=17.5125 Z=0
    g9: GeomPoint X=0 Y=20.6875 Z=0
    g10: GeomPoint X=0 Y=119.087 Z=0
    g11: GeomPoint X=-113 Y=115.912 Z=0
  constraints (28):
    c: Coincident(g0,g1)
    c: Coincident(g1,g2)
    c: Coincident(g2,g3)
    c: Coincident(g3,g0)
    c: Vertical(g0)
    c: Vertical(g2)
    c: Horizontal(g1)
    c: Horizontal(g3)
    c: Coincident(g4,g5)
    c: Coincident(g5,g6)
    c: Coincident(g6,g7)
    c: Coincident(g7,g4)
    c: Vertical(g4)
    c: Vertical(g6)
    c: Horizontal(g5)
    c: Horizontal(g7)
    c: Equal(g2,g-6)
    c: Equal(g6,g2)
    c: Symmetric(g0,g0,g8)
    c: Symmetric(g3,g3,g9)
    c: PointOnObject(g9,g-2)
    c: Symmetric(g7,g7,g10)
    c: Symmetric(g4,g4,g11)
    c: PointOnObject(g10,g-2)
    c: DistanceY(g-3,g8) = 111.1
    c: DistanceX(g1,g1) = 130
    c: DistanceY(g-3,g11) = 209.5
    c: DistanceX(g5,g5) = 226
FEATURE [PartDesign::Pad] Pad033
  BaseFeature = -> Pad032
  Direction = (0,0,-1)
  Length = 8
  Length2 = 10
  Profile = -> Sketch050
  ReferenceAxis = -> Sketch050 [N_Axis]
  Refine = true
  Reversed = true
  Suppressed = false
  Type = 0
FEATURE [PartDesign::Body] Body001  label="Body"
  AllowCompound = false
  Group = -> [Sketch003,Pad,Sketch004,Pocket,Sketch005,Pad001,Sketch006,Pad002,Sketch007,Pocket001,Sketch008,Pad003,Sketch009,Pad004,Sketch010,Pocket002,Sketch011,Pad005,Sketch012,Pad006,Sketch015,Pad009,Sketch046,Sketch047,Pad030,Sketch048,Pad031,Sketch049,Pad032,Sketch050,Pad033]
  Origin = -> Origin001
  Tip = -> Pad033
COMPONENT P1 — recipe-attached ("neck001", modeled in this document).
Construction recipe (the document's own serialized feature program — sketch geometry with constraints, then the solid features built on it; lengths are millimeters unless a unit is written):

FEATURE [Sketcher::SketchObject] Sketch013
  ArcFitTolerance = 1e-06
  AttachmentSupport = -> [XY_Plane004]
  FullyConstrained = false
  MakeInternals = false
  MapMode = 5
  sketch-geometry (22):
    g0-g3: Circle [constr] x4 (B-spline internal-alignment scaffolding for g4; pole/knot coordinates omitted)
    g4: BSplineCurve PolesCount=14 KnotsCount=2 Degree=13 IsPeriodic=0
    g5: GeomPoint [constr] X=-690.982 Y=-223.281 Z=0
    g6: GeomPoint [constr] X=-657.619 Y=129.643 Z=0
    g7-g16: Circle [constr] x10 (B-spline internal-alignment scaffolding for g4; pole/knot coordinates omitted)
    g17: LineSegment StartX=-657.619 StartY=129.643 StartZ=0 EndX=-648.236 EndY=131.188 EndZ=0
    g18: LineSegment StartX=-648.236 StartY=131.188 StartZ=0 EndX=-626.176 EndY=6.08216 EndZ=0
    g19: LineSegment StartX=-626.176 StartY=6.08216 StartZ=0 EndX=-626.176 EndY=-236.32 EndZ=0
    g20: LineSegment StartX=-626.176 StartY=-236.32 StartZ=0 EndX=-690.982 EndY=-236.32 EndZ=0
    g21: LineSegment StartX=-690.982 StartY=-236.32 StartZ=0 EndX=-690.982 EndY=-223.281 EndZ=0
  constraints (37):
    c: Weight(g0) = 1
    c: Equal(g0,g1)
    c: Equal(g0,g2)
    c: Equal(g0,g3)
    c: InternalAlignment(g0-g3 -> g4) x4
    c: InternalAlignment(g5,g4)
    c: InternalAlignment(g6,g4)
    c: InternalAlignment(g7,g4)
    c: Equal(g7,g0)
    c: InternalAlignment(g8,g4)
    c: Equal(g8,g0)
    c: InternalAlignment(g9,g4)
    c: Equal(g9,g0)
    c: InternalAlignment(g10,g4)
    c: Equal(g10,g0)
    c: InternalAlignment(g11,g4)
    c: Equal(g11,g0)
    c: InternalAlignment(g12,g4)
    c: Equal(g12,g0)
    c: InternalAlignment(g13,g4)
    c: Equal(g13,g0)
    c: InternalAlignment(g14,g4)
    c: Equal(g14,g0)
    c: InternalAlignment(g15,g4)
    c: Equal(g15,g0)
    c: InternalAlignment(g16,g4)
    c: Equal(g16,g0)
    c: Coincident(g17,g4)
    c: Coincident(g18,g17)
    c: Coincident(g19,g18)
    c: Vertical(g19)
    c: Coincident(g20,g19)
    c: Horizontal(g20)
    c: Coincident(g21,g20)
    c: Coincident(g21,g4)
    c: Vertical(g21)
    c: Angle(g18,g19) = 2.96706
FEATURE [PartDesign::Pad] Pad007
  Direction = (0,0,1)
  Length = 44.45
  Length2 = 10
  Profile = -> Sketch013
  ReferenceAxis = -> Sketch013 [N_Axis]
  Refine = true
  Reversed = true
  Suppressed = false
  Type = 0
FEATURE [Sketcher::SketchObject] Sketch014
  ArcFitTolerance = 1e-06
  AttachmentSupport = -> [Pad007]
  ExternalGeometry = -> [Pad007]
  FullyConstrained = true
  MakeInternals = false
  MapMode = 5
  Placement = pos=(0,-236.32,0) rot=(1,0,0;1.5708rad)
  sketch-geometry (5):
    g0: LineSegment StartX=-626.176 StartY=-12.7 StartZ=0 EndX=-689.676 EndY=-12.7 EndZ=0
    g1: LineSegment StartX=-689.676 StartY=-12.7 StartZ=0 EndX=-689.676 EndY=-31.75 EndZ=0
    g2: LineSegment StartX=-689.676 StartY=-31.75 StartZ=0 EndX=-626.176 EndY=-31.75 EndZ=0
    g3: LineSegment StartX=-626.176 StartY=-31.75 StartZ=0 EndX=-626.176 EndY=-12.7 EndZ=0
    g4: GeomPoint X=-626.176 Y=-22.225 Z=0
  constraints (12):
    c: Coincident(g0,g1)
    c: Coincident(g1,g2)
    c: Coincident(g2,g3)
    c: Coincident(g3,g0)
    c: Horizontal(g0)
    c: Horizontal(g2)
    c: Vertical(g1)
    c: Vertical(g3)
    c: Symmetric(g3,g3,g4)
    c: Symmetric(g-3,g-4,g4)
    c: DistanceX(g0,g0) = 63.5
    c: DistanceY(g1,g1) = 19.05
FEATURE [PartDesign::Pad] Pad008
  BaseFeature = -> Pad007
  Direction = (0,-1,2e-16)
  Length = 15.875
  Length2 = 10
  Profile = -> Sketch014
  ReferenceAxis = -> Sketch014 [N_Axis]
  Refine = true
  Suppressed = false
  Type = 0
FEATURE [Sketcher::SketchObject] Sketch016
  ArcFitTolerance = 1e-06
  AttachmentSupport = -> [Pad008]
  ExternalGeometry = -> [Pad008]
  FullyConstrained = true
  MakeInternals = false
  MapMode = 5
  Placement = pos=(-606.255,-106.899,0) rot=(0.510274,0.60812,0.60812;2.19793rad)
  sketch-geometry (13):
    g0: GeomPoint X=114.724 Y=-22.225 Z=0
    g1: GeomPoint X=114.724 Y=-6.35 Z=0
    g2: GeomPoint X=114.724 Y=-38.1 Z=0
    g3: LineSegment [constr] StartX=114.724 StartY=-6.35 StartZ=0 EndX=198.824 EndY=-6.35 EndZ=0
    g4: LineSegment [constr] StartX=114.724 StartY=-38.1 StartZ=0 EndX=198.824 EndY=-38.1 EndZ=0
    g5: GeomPoint [constr] X=160.724 Y=-6.35 Z=0
    g6: GeomPoint [constr] X=160.724 Y=-38.1 Z=0
    g7: LineSegment [constr] StartX=160.724 StartY=-6.35 StartZ=0 EndX=160.724 EndY=-38.1 EndZ=0
    g8: LineSegment [constr] StartX=198.824 StartY=-6.35 StartZ=0 EndX=198.824 EndY=-38.1 EndZ=0
    g9: Circle CenterX=198.824 CenterY=-6.35 CenterZ=0 NormalX=0 NormalY=0 NormalZ=1 AngleXU=0 Radius=4.76
    g10: Circle CenterX=160.724 CenterY=-6.35 CenterZ=0 NormalX=0 NormalY=0 NormalZ=1 AngleXU=0 Radius=4.76
    g11: Circle CenterX=198.824 CenterY=-38.1 CenterZ=0 NormalX=0 NormalY=0 NormalZ=1 AngleXU=0 Radius=4.76
    g12: Circle CenterX=160.724 CenterY=-38.1 CenterZ=0 NormalX=0 NormalY=0 NormalZ=1 AngleXU=0 Radius=4.76
  constraints (26):
    c: Symmetric(g-3,g-3,g0)
    c: PointOnObject(g1,g-3)
    c: Symmetric(g2,g1,g0)
    c: DistanceY(g2,g1) = 31.75
    c: Coincident(g3,g1)
    c: Horizontal(g3)
    c: Coincident(g4,g2)
    c: Horizontal(g4)
    c: PointOnObject(g5,g3)
    c: PointOnObject(g6,g4)
    c: Coincident(g7,g5)
    c: Coincident(g7,g6)
    c: Vertical(g7)
    c: Coincident(g8,g3)
    c: Coincident(g8,g4)
    c: Vertical(g8)
    c: DistanceX(g5,g1) = -46
    c: DistanceX(g3,g1) = -84.1
    c: Coincident(g9,g3)
    c: Coincident(g11,g4)
    c: Coincident(g12,g6)
    c: Equal(g9,g10)
    c: Equal(g10,g12)
    c: Equal(g12,g11)
    c: Diameter(g11) = 9.52
    c: Coincident(g10,g5)
FEATURE [Sketcher::SketchObject] Sketch017
  ArcFitTolerance = 1e-06
  AttachmentSupport = -> [Pad008]
  ExternalGeometry = -> [Pad008,Sketch016]
  FullyConstrained = false
  MakeInternals = false
  MapMode = 5
  Placement = pos=(-606.255,-106.899,0) rot=(0.510274,0.60812,0.60812;2.19793rad)
  sketch-geometry (15):
    g0: GeomPoint X=114.724 Y=-22.225 Z=0
    g1: GeomPoint X=114.724 Y=-3.97 Z=0
    g2: GeomPoint X=114.724 Y=-40.48 Z=0
    g3: LineSegment StartX=114.724 StartY=-3.97 StartZ=0 EndX=160.724 EndY=2.83375 EndZ=0
    g4: LineSegment StartX=114.724 StartY=-40.48 StartZ=0 EndX=160.724 EndY=-47.2838 EndZ=0
    g5: LineSegment [constr] StartX=160.724 StartY=2.83375 StartZ=0 EndX=160.724 EndY=-47.2838 EndZ=0
    g6: GeomPoint [constr] X=160.724 Y=-22.225 Z=0
    g7: LineSegment StartX=160.724 StartY=2.83375 StartZ=0 EndX=237.085 EndY=4.80349 EndZ=0
    g8: LineSegment StartX=160.724 StartY=-47.2838 StartZ=0 EndX=237.085 EndY=-49.2535 EndZ=0
    g9: GeomPoint X=241.76 Y=-22.225 Z=0
    g10: LineSegment [constr] StartX=237.085 StartY=4.80349 StartZ=0 EndX=237.085 EndY=-49.2535 EndZ=0
    g11: GeomPoint [constr] X=237.085 Y=-22.225 Z=0
    g12: ArcOfCircle CenterX=309.253 CenterY=3.368 CenterZ=0 NormalX=0 NormalY=0 NormalZ=1 AngleXU=0 Radius=72.1831 StartAngle=3.1217 EndAngle=3.50403
    g13: ArcOfCircle CenterX=309.253 CenterY=-47.818 CenterZ=0 NormalX=0 NormalY=0 NormalZ=1 AngleXU=0 Radius=72.1831 StartAngle=2.77915 EndAngle=3.16148
    g14: LineSegment StartX=114.724 StartY=-3.97 StartZ=0 EndX=114.724 EndY=-40.48 EndZ=0
  constraints (27):
    c: Symmetric(g-3,g-3,g0)
    c: PointOnObject(g1,g-3)
    c: Symmetric(g1,g2,g0)
    c: DistanceY(g2,g1) = 36.51
    c: Coincident(g3,g1)
    c: Coincident(g4,g2)
    c: Coincident(g5,g3)
    c: Coincident(g5,g4)
    c: Vertical(g5)
    c: Symmetric(g5,g5,g6)
    c: Symmetric(g-4,g-7,g6)
    c: Coincident(g7,g3)
    c: Coincident(g8,g4)
    c: Horizontal(g0,g9)
    c: Coincident(g10,g7)
    c: Coincident(g10,g8)
    c: Vertical(g10)
    c: Symmetric(g10,g10,g11)
    c: Horizontal(g11,g9)
    c: Coincident(g12,g7)
    c: Coincident(g12,g9)
    c: Coincident(g13,g9)
    c: Coincident(g13,g8)
    c: Equal(g13,g12)
    c: PointOnObject(g9,g-8)
    c: Coincident(g14,g1)
    c: Coincident(g14,g2)
FEATURE [Sketcher::SketchObject] Sketch018
  ArcFitTolerance = 1e-06
  AttachmentSupport = -> [Pad008]
  ExternalGeometry = -> [Pad008]
  FullyConstrained = true
  MakeInternals = false
  MapMode = 5
  Placement = pos=(-38.1526,231.663,0) rot=(-0.057741,0.705927,0.705927;3.25695rad)
  sketch-geometry (4):
    g0: LineSegment StartX=627.811 StartY=0 StartZ=0 EndX=616.865 EndY=0 EndZ=0
    g1: LineSegment StartX=616.865 StartY=0 StartZ=0 EndX=616.865 EndY=-44.45 EndZ=0
    g2: LineSegment StartX=616.865 StartY=-44.45 StartZ=0 EndX=627.811 EndY=-44.45 EndZ=0
    g3: LineSegment StartX=627.811 StartY=-44.45 StartZ=0 EndX=627.811 EndY=0 EndZ=0
  constraints (10):
    c: Coincident(g0,g1)
    c: Coincident(g1,g2)
    c: Coincident(g2,g3)
    c: Coincident(g3,g0)
    c: Horizontal(g0)
    c: Horizontal(g2)
    c: Vertical(g1)
    c: Vertical(g3)
    c: Coincident(g0,g-4)
    c: Coincident(g1,g-5)
FEATURE [PartDesign::Pocket] Pocket003
  BaseFeature = -> Pad008
  Direction = (0.162501,-0.986708,0)
  Length = 20
  Length2 = 5
  Profile = -> Sketch018
  ReferenceAxis = -> Sketch018 [N_Axis]
  Refine = true
  Suppressed = false
  Type = 0
FEATURE [PartDesign::Pad] Pad010
  BaseFeature = -> Pocket003
  Direction = (0.984808,0.173648,2e-16)
  Length = 12
  Length2 = 10
  Profile = -> Sketch017
  ReferenceAxis = -> Sketch017 [N_Axis]
  Refine = true
  Reversed = true
  Suppressed = false
  Type = 0
FEATURE [Sketcher::SketchObject] Sketch019
  ArcFitTolerance = 1e-06
  AttachmentSupport = -> [Pad010]
  ExternalGeometry = -> [Sketch017,Pad010]
  FullyConstrained = true
  MakeInternals = false
  MapMode = 5
  Placement = pos=(-606.255,-106.899,0) rot=(0.510274,0.60812,0.60812;2.19793rad)
  sketch-geometry (3):
    g0: LineSegment StartX=160.724 StartY=2.83375 StartZ=0 EndX=114.724 EndY=-3.97 EndZ=0
    g1: LineSegment StartX=114.724 StartY=-3.97 StartZ=0 EndX=-123.995 EndY=0 EndZ=0
    g2: LineSegment StartX=-123.995 StartY=0 StartZ=0 EndX=160.724 EndY=2.83375 EndZ=0
  constraints (6):
    c: Coincident(g-3,g0)
    c: Coincident(g0,g-3)
    c: Coincident(g0,g1)
    c: Coincident(g1,g-4)
    c: Coincident(g1,g2)
    c: Coincident(g2,g0)
FEATURE [PartDesign::Pocket] Pocket004
  BaseFeature = -> Pad010
  Direction = (-0.984808,-0.173648,0)
  Length = 500
  Length2 = 5
  Profile = -> Sketch019
  ReferenceAxis = -> Sketch019 [N_Axis]
  Refine = true
  Suppressed = false
  Type = 0
FEATURE [PartDesign::Hole] Hole
  BaseFeature = -> Pocket004
  CustomThreadClearance = 0
  Depth = 25
  DepthType = 0
  Diameter = 6
  DrillForDepth = false
  DrillPoint = 1
  DrillPointAngle = 118
  HoleCutCountersinkAngle = 90
  HoleCutCustomValues = false
  HoleCutDepth = 0
  HoleCutDiameter = 6.1
  HoleCutType = 0
  ModelThread = false
  Profile = -> Sketch016
  Refine = true
  Suppressed = false
  Tapered = false
  TaperedAngle = 90
  ThreadClass = 0
  ThreadDepth = 25
  ThreadDepthType = 0
  ThreadDirection = 0
  ThreadFit = 0
  ThreadSize = 0
  ThreadType = 0
  Threaded = false
  UseCustomThreadClearance = false
FEATURE [Sketcher::SketchObject] Sketch020
  ArcFitTolerance = 1e-06
  AttachmentSupport = -> [Hole]
  ExternalGeometry = -> [Sketch017,Hole]
  FullyConstrained = true
  MakeInternals = false
  MapMode = 5
  Placement = pos=(-606.255,-106.899,0) rot=(0.510274,0.60812,0.60812;2.19793rad)
  sketch-geometry (3):
    g0: LineSegment StartX=114.724 StartY=-40.48 StartZ=0 EndX=-123.995 EndY=-44.45 EndZ=0
    g1: LineSegment StartX=-123.995 StartY=-44.45 StartZ=0 EndX=160.724 EndY=-47.2838 EndZ=0
    g2: LineSegment StartX=160.724 StartY=-47.2838 StartZ=0 EndX=114.724 EndY=-40.48 EndZ=0
  constraints (6):
    c: Coincident(g-3,g0)
    c: Coincident(g0,g-4)
    c: Coincident(g0,g1)
    c: Coincident(g1,g-3)
    c: Coincident(g1,g2)
    c: Coincident(g2,g0)
FEATURE [PartDesign::Pocket] Pocket005
  BaseFeature = -> Hole
  Direction = (-0.984808,-0.173648,0)
  Length = 500
  Length2 = 5
  Profile = -> Sketch020
  ReferenceAxis = -> Sketch020 [N_Axis]
  Refine = true
  Suppressed = false
  Type = 0
FEATURE [Sketcher::SketchObject] Sketch021
  ArcFitTolerance = 1e-06
  AttachmentSupport = -> [Pocket005]
  ExternalGeometry = -> [Pocket005]
  FullyConstrained = true
  MakeInternals = false
  MapMode = 5
  Placement = pos=(-690.982,0,0) rot=(0.57735,-0.57735,-0.57735;2.0944rad)
  sketch-geometry (4):
    g0: LineSegment StartX=236.32 StartY=-0.187148 StartZ=0 EndX=223.281 EndY=-0.187148 EndZ=0
    g1: LineSegment StartX=223.281 StartY=-0.187148 StartZ=0 EndX=223.281 EndY=-44.0493 EndZ=0
    g2: LineSegment StartX=223.281 StartY=-44.0493 StartZ=0 EndX=236.32 EndY=-44.0493 EndZ=0
    g3: LineSegment StartX=236.32 StartY=-44.0493 StartZ=0 EndX=236.32 EndY=-0.187148 EndZ=0
  constraints (10):
    c: Coincident(g0,g1)
    c: Coincident(g1,g2)
    c: Coincident(g2,g3)
    c: Coincident(g3,g0)
    c: Horizontal(g0)
    c: Horizontal(g2)
    c: Vertical(g1)
    c: Vertical(g3)
    c: Coincident(g0,g-4)
    c: Coincident(g1,g-3)
FEATURE [PartDesign::Pad] Pad011
  BaseFeature = -> Pocket005
  Direction = (-1,0,0)
  Length = 2
  Length2 = 10
  Profile = -> Sketch021
  ReferenceAxis = -> Sketch021 [N_Axis]
  Refine = true
  Suppressed = false
  Type = 0
FEATURE [Sketcher::SketchObject] Sketch022
  ArcFitTolerance = 1e-06
  AttachmentSupport = -> [Pad011]
  ExternalGeometry = -> [Pad011,Sketch017]
  FullyConstrained = false
  MakeInternals = false
  MapMode = 5
  Placement = pos=(-626.176,0,0) rot=(0.57735,0.57735,0.57735;2.0944rad)
  sketch-geometry (7):
    g0: LineSegment StartX=2.91216 StartY=-3.91808 StartZ=0 EndX=-303.442 EndY=1.09931 EndZ=0
    g1: LineSegment StartX=2.91216 StartY=-40.5319 StartZ=0 EndX=-303.442 EndY=-45.5493 EndZ=0
    g2: GeomPoint X=-309.663 Y=-22.225 Z=0
    g3: GeomPoint X=6.08216 Y=-22.225 Z=0
    g4: ArcOfCircle CenterX=-336.111 CenterY=-2.67954 CenterZ=0 NormalX=0 NormalY=0 NormalZ=1 AngleXU=0 Radius=32.8871 StartAngle=5.64676 EndAngle=6.39834
    g5: ArcOfCircle CenterX=-336.111 CenterY=-41.7705 CenterZ=0 NormalX=0 NormalY=0 NormalZ=1 AngleXU=0 Radius=32.8871 StartAngle=6.16803 EndAngle=6.91961
    g6: LineSegment StartX=2.91216 StartY=-3.91808 StartZ=0 EndX=2.91216 EndY=-40.5319 EndZ=0
  constraints (16):
    c: PointOnObject(g-3,g0)
    c: PointOnObject(g-5,g1)
    c: Symmetric(g-4,g-4,g3)
    c: Horizontal(g3,g2)
    c: Vertical(g0,g1)
    c: Coincident(g4,g0)
    c: Coincident(g4,g2)
    c: Coincident(g5,g2)
    c: Coincident(g5,g1)
    c: Equal(g5,g4)
    c: PointOnObject(g0,g-3)
    c: PointOnObject(g1,g-5)
    c: Coincident(g6,g0)
    c: Coincident(g6,g1)
    c: Vertical(g6)
    c: DistanceX(g0,g-4) = 3.17
FEATURE [PartDesign::Pad] Pad012
  BaseFeature = -> Pad011
  Direction = (1,0,0)
  Length = 6.25
  Length2 = 10
  Profile = -> Sketch022
  ReferenceAxis = -> Sketch022 [N_Axis]
  Refine = true
  Suppressed = false
  Type = 0
FEATURE [Sketcher::SketchObject] Sketch023
  ArcFitTolerance = 1e-06
  AttachmentSupport = -> [Pad012]
  ExternalGeometry = -> [Pad012,Sketch017]
  FullyConstrained = true
  MakeInternals = false
  MapMode = 5
  Placement = pos=(-626.176,0,0) rot=(0.57735,0.57735,0.57735;2.0944rad)
  sketch-geometry (4):
    g0: LineSegment StartX=2.91216 StartY=-3.91808 StartZ=0 EndX=2.91216 EndY=-40.5319 EndZ=0
    g1: LineSegment StartX=2.91216 StartY=-40.5319 StartZ=0 EndX=6.08216 EndY=-40.48 EndZ=0
    g2: LineSegment StartX=6.08216 StartY=-40.48 StartZ=0 EndX=6.08216 EndY=-3.97 EndZ=0
    g3: LineSegment StartX=6.08216 StartY=-3.97 StartZ=0 EndX=2.91216 EndY=-3.91808 EndZ=0
  constraints (8):
    c: Coincident(g-3,g0)
    c: Coincident(g0,g-3)
    c: Coincident(g0,g1)
    c: Coincident(g1,g-4)
    c: Coincident(g1,g2)
    c: Coincident(g2,g-4)
    c: Coincident(g2,g3)
    c: Coincident(g3,g0)
FEATURE [PartDesign::Pad] Pad013
  BaseFeature = -> Pad012
  Direction = (1,0,0)
  Length = 9
  Length2 = 10
  Profile = -> Sketch023
  ReferenceAxis = -> Sketch023 [N_Axis]
  Refine = true
  Suppressed = false
  Type = 0
FEATURE [PartDesign::Body] Body002
  AllowCompound = false
  Group = -> [Sketch013,Pad007,Sketch014,Pad008,Sketch016,Sketch017,Sketch018,Pocket003,Pad010,Sketch019,Pocket004,Hole,Sketch020,Pocket005,Sketch021,Pad011,Sketch022,Pad012,Sketch023,Pad013]
  Origin = -> Origin004
  Tip = -> Pad013
PROVENANCE & LICENSES
A FreeCAD (.FCStd) document from a public repository crawl; recipes are the document's own serialized feature recipes (and, for linked parts, companion documents' recipes).
License: as declared in the source repository (recorded in the dataset sidecar).
